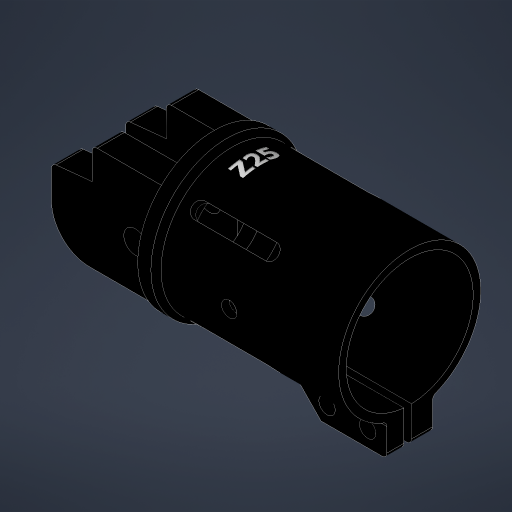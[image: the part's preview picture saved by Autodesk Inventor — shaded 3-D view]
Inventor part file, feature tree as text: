
AUTODESK INVENTOR PART (.ipt)
format: ipt  version: 2024.1 (Build 281209000, 209)  size: 544,768 bytes
history: native  units: mm
features: extrude x15, fillet x4, thread x4, sketch x4, plane x3, projected_geometry x2, chamfer x1, other x1, revolve x1, pattern_circular x1, emboss x1
ambient origin geometry x8: Origin, YZ Plane, XZ Plane, XY Plane, X Axis, Y Axis, Z Axis, Center Point
bodies: Solid1 (feature_tree)
feature tree (37):
  extrude  "Extrusion1"  Depth=38.6mm TaperAngle=0.0deg
  extrude  "Extrusion2"  Depth=30.0mm
  chamfer  "Chamfer1"  Distance=36.0mm
  extrude  "Extrusion3"  Depth=25.0mm
  extrude  "Extrusion4"  Depth=14.0mm
  extrude  "Extrusion5"  Depth=14.0mm TaperAngle=0.0deg
  fillet  "Fillet1"  Radius=5.5mm
  extrude  "Extrusion6"  Depth=14.0mm
  extrude  "Extrusion7"  Depth=14.0mm
  extrude  "Extrusion8"  Depth=14.0mm
  fillet  "Fillet2"  Radius=4.0mm
  extrude  "Extrusion10"  Depth=14.0mm TaperAngle=0.0deg
  plane  "Work Plane1"
  other  "Work Axis1"
  revolve  "Revolution1"  [1 undecoded]
  extrude  "Extrusion11"  Depth=14.0mm
  extrude  "Extrusion12"  Depth=14.0mm
  extrude  "Extrusion13"  Depth=14.0mm
  fillet  "Fillet3"  Radius=29.0mm
  fillet  "Fillet4"  Radius=3.0mm
  extrude  "Extrusion14"  Depth=14.0mm
  extrude  "Extrusion15"  Depth=14.0mm
  plane  "Work Plane2"
  extrude  "Extrusion16"  Depth=14.0mm
  pattern_circular  "Circular Pattern1"  [2 undecoded]
  plane  "Work Plane3"
  emboss  "Emboss1"
  thread  "Thread4"  [1 undecoded]
  thread  "Thread5"  [1 undecoded]
  thread  "Thread6"  [1 undecoded]
  thread  "Thread7"  [1 undecoded]
  sketch  "Sketch5"  dims[d0=30.0mm d1=38.6mm d2=0.0mm]
  sketch  "Sketch7"  dims[d3=28.0mm d4=30.0mm d5=36.0mm d6=0.0mm]
  sketch  "Sketch11"  dims[d7=1.0mm d8=2.0mm d9=45.0deg d10=25.0mm]
  projected_geometry  "Projected Loop1"
  projected_geometry  "Projected Loop2"
  sketch  "Sketch18"  dims[d11=36.0mm d12=0.0mm d13=14.0mm d14=36.0mm d15=0.0mm d16=5.5mm d17=9.0mm d18=5.5mm d19=9.0mm d20=4.0mm d21=19.0mm d22=0.0mm d23=1.0mm d27=3.35mm d28=1.5mm d29=9.0mm d30=29.0mm d31=0.0mm d32=3.0mm d33=3.25mm d34=3.8mm d35=3.0mm d36=8.0mm d37=0.0mm d38=0.0mm d39=3.2mm d40=3.2mm d41=4.0mm d42=0.0mm d43=1.0mm d48=5.75mm d49=5.75mm d50=19.0mm d51=0.0mm d52=14.0mm d53=10.0mm d54=10.0mm d55=7.504916mm d56=9.25mm d57=21.0mm d58=5.375mm d59=5.375mm d60=21.0mm d61=22.0mm d62=0.0mm d63=5.5mm d64=8.75mm d65=0.0mm d66=0.0mm d67=4.5mm d68=14.0mm d69=6.2mm d70=14.0mm d71=0.0mm d72=0.0mm d73=7.5mm d74=1.0mm d75=3.0mm d76=3.0mm d77=14.0mm d78=3.5mm d79=5.5mm d80=3.0mm d81=0.0mm d82=17.0mm d83=17.0mm d84=3.0mm d85=0.0mm d86=0.0mm d87=45.0deg d88=17.5mm d89=14.0mm d90=3.0mm d91=0.0mm d92=0.0mm d93=40.0mm d94=360.0deg d96=14.0mm d97=0.1mm d98=0.0mm d105=5.375mm d106=0.0mm d107=5.375mm d108=0.0mm d109=3.25mm d110=4.15mm d111=0.0mm d112=4.15mm d113=0.0mm d46=0.5mm d47=0.872665mm]
note: 7 required parameter values undecoded (feature->parameter linkage not recoverable at this tier; creation-order binding heuristic only, values carry confidence <= 0.55)